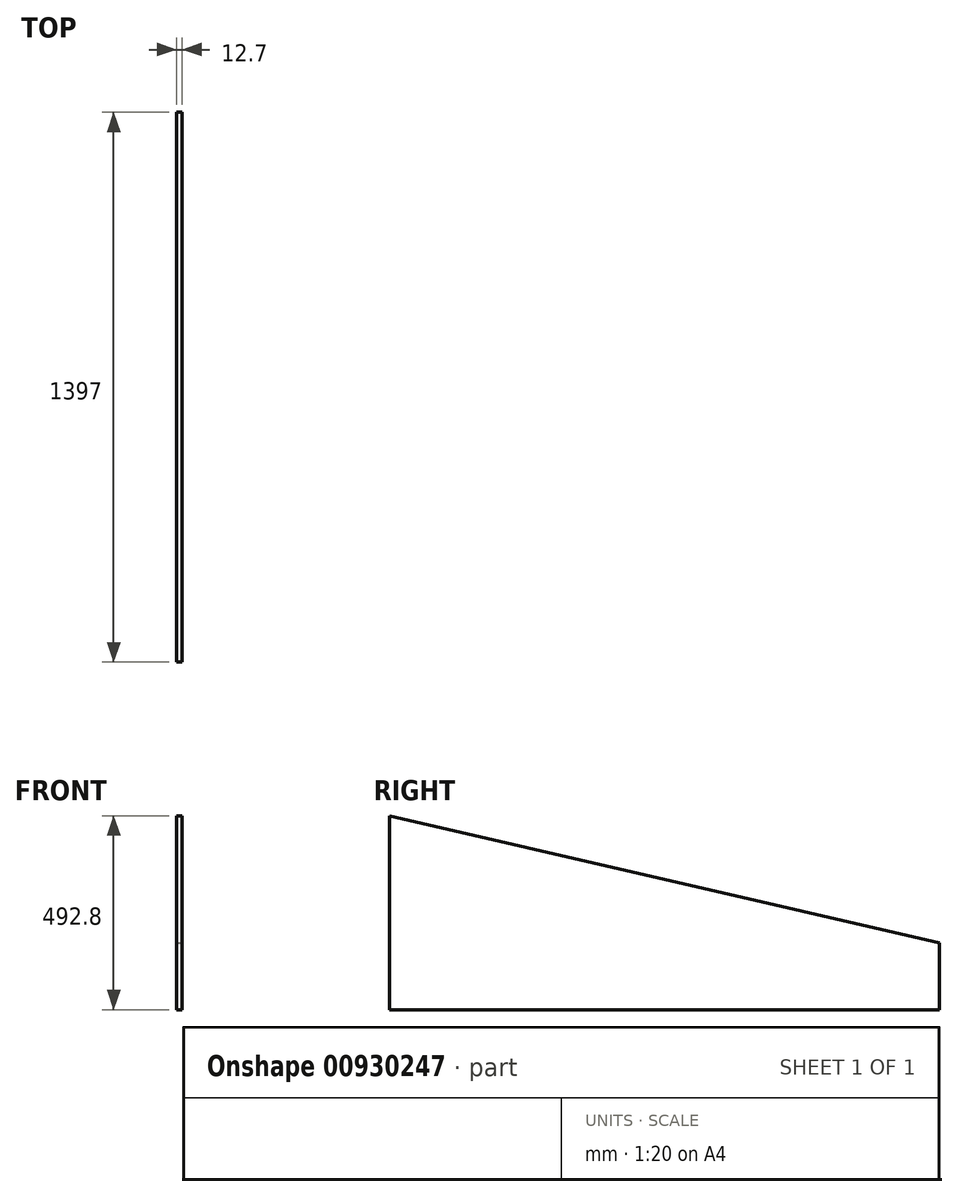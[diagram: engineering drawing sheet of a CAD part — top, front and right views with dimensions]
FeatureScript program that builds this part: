
annotation { "Feature Type Name" : "Feature", "Feature Type Description" : "" }
export const myFeature = defineFeature(function(context is Context, id is Id, definition is map)
    precondition{}
    {
        {
            var Q0;
            Q0=qCreatedBy(makeId("Right.planeOp"),FACE);
            var sketch = newSketch(context, id + "F0", { "sketchPlane" : qUnion([Q0])});
            skLineSegment(sketch, "E0", {"start": v(0, 0) * mm, "end": v(2359.6, 0) * mm});
            skLineSegment(sketch, "E1", {"start": v(2359.6, 0) * mm, "end": v(0, 544.76) * mm});
            skLineSegment(sketch, "E2", {"start": v(0, 544.76) * mm, "end": v(0, 0) * mm});
            skSolve(sketch);
        }
        {
            var Q0;
            Q0=qSketchRegion(id+"F0",true);
            extrude(context, id + "F1", {"entities" : qUnion([Q0]), "endBound" : BoundingType.SYMMETRIC, "depth" : 12.7 * mm});
        }
        {
            var Q0;
            Q0=makeQuery(id+"F1.opExtrude","CAP_FACE",FACE,{"disambiguationData":[OSD([sQuery(id+"F0.wireOp",EDGE,"E0"),sQuery(id+"F0.wireOp",EDGE,"E1"),sQuery(id+"F0.wireOp",EDGE,"E2")])],"isStart":false});
            var sketch = newSketch(context, id + "F2", { "sketchPlane" : qUnion([Q0])});
            skLineSegment(sketch, "E3", {"start": v(225.04, 0) * mm, "end": v(225.04, 492.8) * mm});
            skLineSegment(sketch, "E4", {"start": v(1622.04, 0) * mm, "end": v(1622.04, 170.28) * mm});
            skSolve(sketch);
        }
        {
            var Q0;
            {var subQ0=sQuery(id+"F2.wireOp",EDGE,"E3");Q0=makeQuery(id+"F2.imprint","IMPRINT",FACE,{"disambiguationData":[TD([[makeQuery(id+"F2.imprint","IMPRINT",EDGE,{"derivedFrom":subQ0}),1.0]])]});}
            var Q1;
            {var subQ0=sQuery(id+"F2.wireOp",EDGE,"E4");Q1=makeQuery(id+"F2.imprint","IMPRINT",FACE,{"disambiguationData":[TD([[makeQuery(id+"F2.imprint","IMPRINT",EDGE,{"derivedFrom":subQ0}),-1.0]])]});}
            extrude(context, id + "F3", {"entities" : qUnion([Q0, Q1]), "operationType" : NewBodyOperationType.REMOVE, "endBound" : BoundingType.THROUGH_ALL, "oppositeDirection" : true, "depth" : 25.4 * mm});
        }
    });
